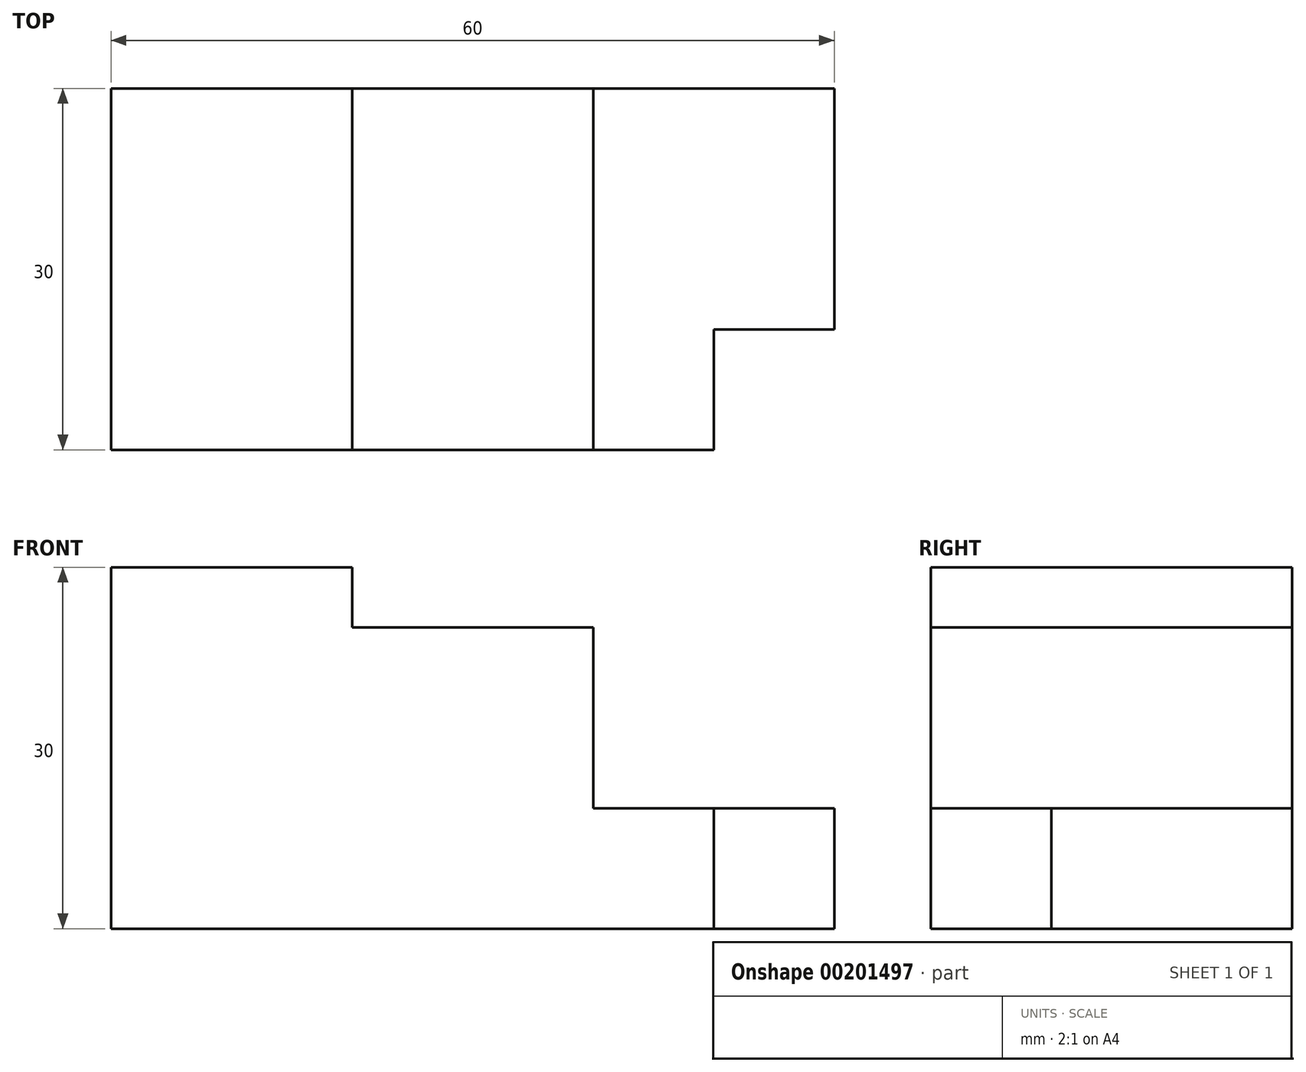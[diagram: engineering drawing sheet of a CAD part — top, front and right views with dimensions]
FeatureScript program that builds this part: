
annotation { "Feature Type Name" : "Feature", "Feature Type Description" : "" }
export const myFeature = defineFeature(function(context is Context, id is Id, definition is map)
    precondition{}
    {
        {
            var Q0;
            Q0=qCreatedBy(makeId("Front.planeOp"),FACE);
            var sketch = newSketch(context, id + "F0", { "sketchPlane" : qUnion([Q0])});
            skLineSegment(sketch, "E0", {"start": v(0, 0) * mm, "end": v(-60, 0) * mm});
            skLineSegment(sketch, "E1", {"start": v(-60, 0) * mm, "end": v(-60, 30) * mm});
            skLineSegment(sketch, "E2", {"start": v(-60, 30) * mm, "end": v(-40, 30) * mm});
            skLineSegment(sketch, "E3", {"start": v(-40, 30) * mm, "end": v(-40, 25) * mm});
            skLineSegment(sketch, "E4", {"start": v(-40, 25) * mm, "end": v(-20, 25) * mm});
            skLineSegment(sketch, "E5", {"start": v(-20, 25) * mm, "end": v(-20, 10) * mm});
            skLineSegment(sketch, "E6", {"start": v(-20, 10) * mm, "end": v(0, 10) * mm});
            skLineSegment(sketch, "E7", {"start": v(0, 10) * mm, "end": v(0, 0) * mm});
            skLineSegment(sketch, "E8", {"start": v(-10, 10) * mm, "end": v(-10, 0) * mm});
            skSolve(sketch);
        }
        {
            var Q0;
            Q0=qSketchRegion(id+"F0",true);
            extrude(context, id + "F1", {"entities" : qUnion([Q0]), "oppositeDirection" : true, "depth" : 30 * mm});
        }
        {
            var Q0;
            {var subQ0=sQuery(id+"F0.wireOp",EDGE,"E7");Q0=makeQuery(id+"F0.imprint","IMPRINT",FACE,{"disambiguationData":[TD([[makeQuery(id+"F0.imprint","IMPRINT",EDGE,{"derivedFrom":subQ0}),-1.0]])]});}
            extrude(context, id + "F2", {"entities" : qUnion([Q0]), "operationType" : NewBodyOperationType.REMOVE, "oppositeDirection" : true, "depth" : 10 * mm});
        }
    });
